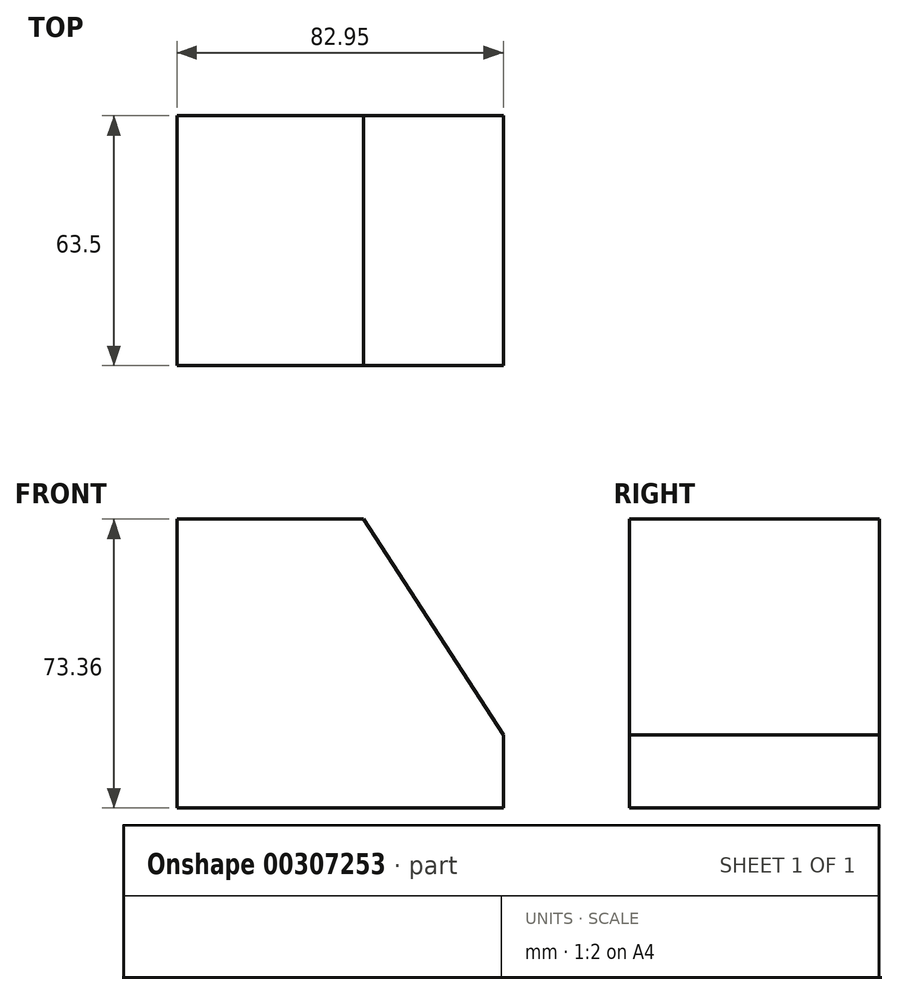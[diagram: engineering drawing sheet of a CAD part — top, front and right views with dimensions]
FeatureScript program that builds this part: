
annotation { "Feature Type Name" : "Feature", "Feature Type Description" : "" }
export const myFeature = defineFeature(function(context is Context, id is Id, definition is map)
    precondition{}
    {
        {
            var Q0;
            Q0=qCreatedBy(makeId("Front.planeOp"),FACE);
            var sketch = newSketch(context, id + "F0", { "sketchPlane" : qUnion([Q0])});
            skLineSegment(sketch, "E0", {"start": v(49.52, -17.49) * mm, "end": v(49.52, -36.06) * mm});
            skLineSegment(sketch, "E1", {"start": v(49.52, -36.06) * mm, "end": v(-33.43, -36.06) * mm});
            skLineSegment(sketch, "E2", {"start": v(-33.43, -36.06) * mm, "end": v(-33.43, 37.3) * mm});
            skLineSegment(sketch, "E3", {"start": v(-33.43, 37.3) * mm, "end": v(13.93, 37.3) * mm});
            skLineSegment(sketch, "E4", {"start": v(13.93, 37.3) * mm, "end": v(49.52, -17.49) * mm});
            skSolve(sketch);
        }
        {
            var Q0;
            Q0=makeQuery(id+"F0.imprint","IMPRINT",FACE,{"disambiguationData":[TD([[makeQuery(id+"F0.imprint","IMPRINT",EDGE,{"derivedFrom":sQuery(id+"F0.wireOp",EDGE,"E0")}),-1.0]])]});
            extrude(context, id + "F1", {"entities" : qUnion([Q0]), "depth" : 63.5 * mm});
        }
    });
